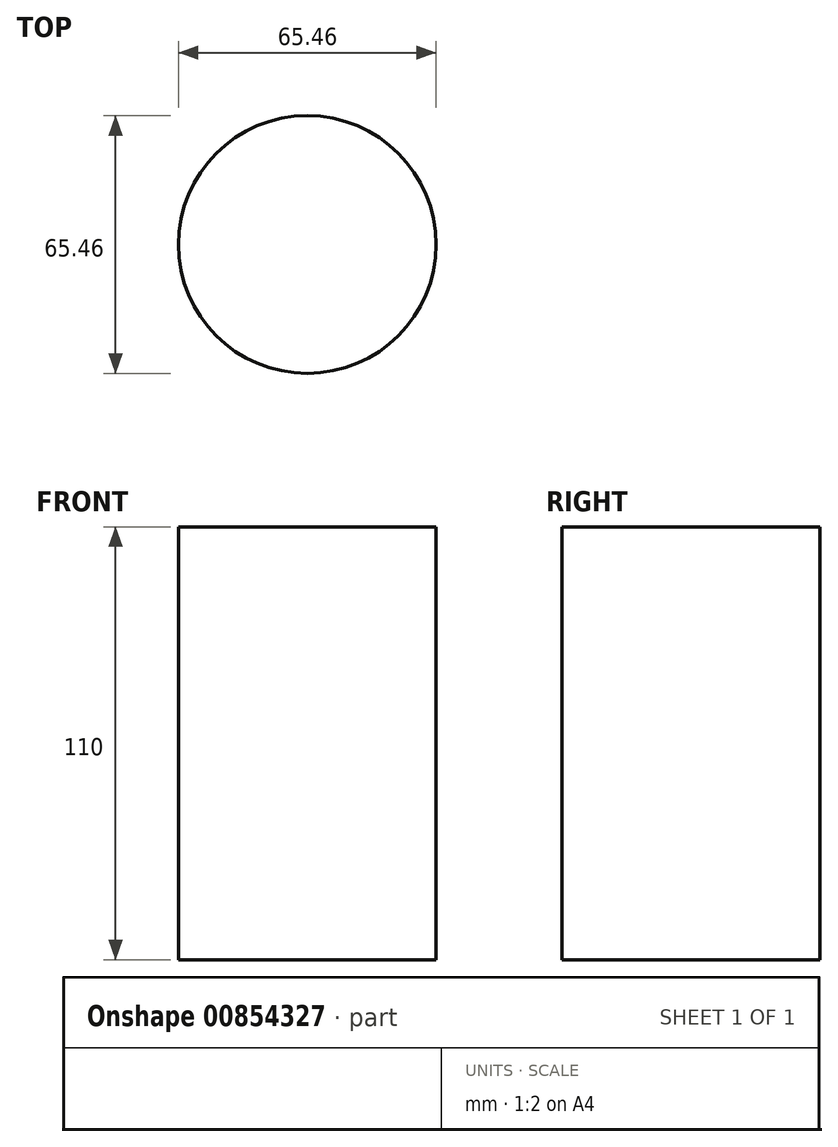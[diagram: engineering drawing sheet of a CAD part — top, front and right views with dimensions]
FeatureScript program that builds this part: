
annotation { "Feature Type Name" : "Feature", "Feature Type Description" : "" }
export const myFeature = defineFeature(function(context is Context, id is Id, definition is map)
    precondition{}
    {
        {
            var Q0;
            Q0=qCreatedBy(makeId("Top.planeOp"),FACE);
            var sketch = newSketch(context, id + "F0", { "sketchPlane" : qUnion([Q0])});
            skCircle(sketch, "E0", {"center": v(0, 0) * mm, "radius": 32.73 * mm});
            skSolve(sketch);
        }
        {
            var Q0;
            Q0=makeQuery(id+"F0.imprint","IMPRINT",FACE,{"disambiguationData":[TD([[makeQuery(id+"F0.imprint","IMPRINT",EDGE,{"derivedFrom":sQuery(id+"F0.wireOp",EDGE,"E0")}),1.0]])]});
            extrude(context, id + "F1", {"entities" : qUnion([Q0]), "depth" : 110 * mm, "offsetDistance" : 25 * mm});
        }
    });
